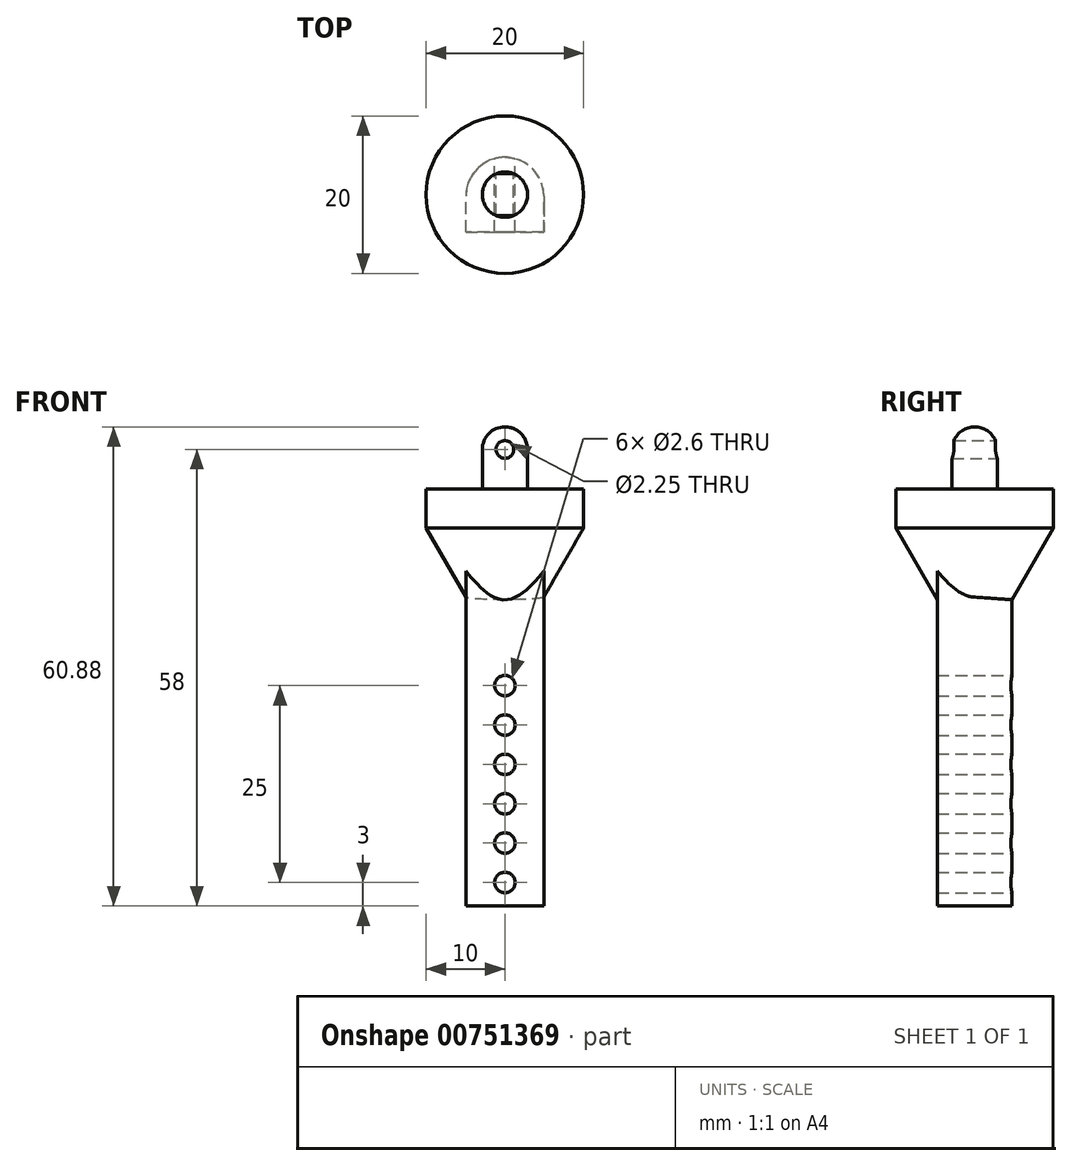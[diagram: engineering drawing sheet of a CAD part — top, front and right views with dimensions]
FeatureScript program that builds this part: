
annotation { "Feature Type Name" : "Feature", "Feature Type Description" : "" }
export const myFeature = defineFeature(function(context is Context, id is Id, definition is map)
    precondition{}
    {
        {
            var Q0;
            Q0=qCreatedBy(makeId("Front.planeOp"),FACE);
            var sketch = newSketch(context, id + "F0", { "sketchPlane" : qUnion([Q0])});
            skLineSegment(sketch, "E0", {"start": v(-4.95, 0) * mm, "end": v(4.95, 0) * mm});
            skPoint(sketch, "E1", {"position": v(0, 0) * mm});
            skLineSegment(sketch, "E2", {"start": v(0, 0) * mm, "end": v(0, 3) * mm, "construction": true});
            skLineSegment(sketch, "E3", {"start": v(0, 3) * mm, "end": v(0, 8) * mm, "construction": true});
            skLineSegment(sketch, "E4", {"start": v(0, 8) * mm, "end": v(0, 13) * mm, "construction": true});
            skLineSegment(sketch, "E5", {"start": v(0, 13) * mm, "end": v(0, 18) * mm, "construction": true});
            skLineSegment(sketch, "E6", {"start": v(0, 18) * mm, "end": v(0, 23) * mm, "construction": true});
            skLineSegment(sketch, "E7", {"start": v(0, 23) * mm, "end": v(0, 28) * mm, "construction": true});
            skLineSegment(sketch, "E8", {"start": v(0, 28) * mm, "end": v(0, 53) * mm, "construction": true});
            skCircle(sketch, "E9", {"center": v(0, 3) * mm, "radius": 1.3 * mm});
            skCircle(sketch, "E10", {"center": v(0, 8) * mm, "radius": 1.3 * mm});
            skCircle(sketch, "E11", {"center": v(0, 13) * mm, "radius": 1.3 * mm});
            skCircle(sketch, "E12", {"center": v(0, 18) * mm, "radius": 1.3 * mm});
            skCircle(sketch, "E13", {"center": v(0, 23) * mm, "radius": 1.3 * mm});
            skCircle(sketch, "E14", {"center": v(0, 28) * mm, "radius": 1.3 * mm});
            skCircle(sketch, "E15", {"center": v(0, 53) * mm, "radius": 1.13 * mm, "construction": true});
            skLineSegment(sketch, "E16", {"start": v(4.95, 0) * mm, "end": v(4.95, 28) * mm});
            skLineSegment(sketch, "E17", {"start": v(4.95, 28) * mm, "end": v(4.95, 33) * mm});
            skLineSegment(sketch, "E18", {"start": v(0, 53) * mm, "end": v(0, 49) * mm, "construction": true});
            skLineSegment(sketch, "E19", {"start": v(-10, 49) * mm, "end": v(10, 49) * mm, "construction": true});
            skPoint(sketch, "E20", {"position": v(0, 49) * mm});
            skLineSegment(sketch, "E21", {"start": v(10, 49) * mm, "end": v(10, 43.83) * mm, "construction": true});
            skLineSegment(sketch, "E22", {"start": v(10, 43.83) * mm, "end": v(4.95, 33) * mm, "construction": true});
            skLineSegment(sketch, "E23", {"start": v(4.95, 33) * mm, "end": v(4.95, 40.7) * mm, "construction": true});
            skLineSegment(sketch, "E24", {"start": v(-2.88, 49) * mm, "end": v(2.88, 49) * mm, "construction": true});
            skLineSegment(sketch, "E25", {"start": v(-2.88, 49) * mm, "end": v(-2.88, 53) * mm, "construction": true});
            skLineSegment(sketch, "E26.MirrorCS", {"start": v(2.88, 49) * mm, "end": v(2.88, 53) * mm, "construction": true});
            skLineSegment(sketch, "E27.MirrorCS", {"start": v(-10, 49) * mm, "end": v(-10, 43.83) * mm, "construction": true});
            skLineSegment(sketch, "E28.MirrorCS", {"start": v(-10, 43.83) * mm, "end": v(-4.95, 33) * mm, "construction": true});
            skLineSegment(sketch, "E29.MirrorCS", {"start": v(-4.95, 28) * mm, "end": v(-4.95, 33) * mm});
            skLineSegment(sketch, "E30.MirrorCS", {"start": v(-4.95, 0) * mm, "end": v(-4.95, 28) * mm});
            skArc(sketch, "E31", {"start": v(2.88, 53) * mm, "mid": v(0, 55.88) * mm, "end": v(-2.88, 53) * mm, "construction": true});
            skLineSegment(sketch, "E32", {"start": v(-4.95, 33) * mm, "end": v(4.95, 33) * mm});
            skSolve(sketch);
        }
        {
            var Q0;
            Q0=makeQuery(id+"F0.imprint","IMPRINT",FACE,{"disambiguationData":[TD([[makeQuery(id+"F0.imprint","IMPRINT",EDGE,{"derivedFrom":sQuery(id+"F0.wireOp",EDGE,"E0")}),1.0]])]});
            extrude(context, id + "F1", {"entities" : qUnion([Q0]), "depth" : 9.5 * mm, "offsetDistance" : 25 * mm});
        }
        {
            var Q0;
            Q0=makeQuery(id+"F1.opExtrude","SWEPT_FACE",FACE,{"disambiguationData":[OSD([sQuery(id+"F0.wireOp",EDGE,"E32")])]});
            var sketch = newSketch(context, id + "F2", { "sketchPlane" : qUnion([Q0])});
            skCircle(sketch, "E33", {"center": v(0, -4.75) * mm, "radius": 10 * mm});
            skPoint(sketch, "E33.centerSnap0", {"position": v(-4.95, -4.75) * mm});
            skCircle(sketch, "E34", {"center": v(0, -4.75) * mm, "radius": 2.88 * mm});
            skSolve(sketch);
        }
        {
            var Q0;
            Q0=makeQuery(id+"F2.imprint","IMPRINT",FACE,{"disambiguationData":[TD([[makeQuery(id+"F2.imprint","IMPRINT",EDGE,{"derivedFrom":sQuery(id+"F2.wireOp",EDGE,"E33")}),1.0]])]});
            var Q1;
            Q1=makeQuery(id+"F2.imprint","IMPRINT",FACE,{"disambiguationData":[TD([[makeQuery(id+"F2.imprint","IMPRINT",EDGE,{"derivedFrom":sQuery(id+"F2.wireOp",EDGE,"E34")}),-1.0]])]});
            extrude(context, id + "F3", {"entities" : qUnion([Q0, Q1]), "operationType" : NewBodyOperationType.ADD, "depth" : 20 * mm, "offsetDistance" : 25 * mm});
        }
        {
            var Q0;
            Q0=makeQuery(id+"F2.imprint","IMPRINT",FACE,{"disambiguationData":[TD([[makeQuery(id+"F2.imprint","IMPRINT",EDGE,{"derivedFrom":sQuery(id+"F2.wireOp",EDGE,"E34")}),1.0]])]});
            extrude(context, id + "F4", {"entities" : qUnion([Q0]), "operationType" : NewBodyOperationType.ADD, "depth" : (25 + (5.75 / 2)) * mm, "offsetDistance" : 25 * mm});
        }
        {
            var Q0;
            Q0=qCreatedBy(makeId("Front.planeOp"),FACE);
            var sketch = newSketch(context, id + "F5", { "sketchPlane" : qUnion([Q0])});
            skLineSegment(sketch, "E35", {"start": v(0, 0) * mm, "end": v(0, 58) * mm, "construction": true});
            skCircle(sketch, "E36", {"center": v(0, 58) * mm, "radius": 1.13 * mm});
            skSolve(sketch);
        }
        {
            var Q0;
            Q0=makeQuery(id+"F5.imprint","IMPRINT",FACE,{"disambiguationData":[TD([[makeQuery(id+"F5.imprint","IMPRINT",EDGE,{"derivedFrom":sQuery(id+"F5.wireOp",EDGE,"E36")}),1.0]])]});
            extrude(context, id + "F6", {"entities" : qUnion([Q0]), "operationType" : NewBodyOperationType.REMOVE, "depth" : 25 * mm, "offsetDistance" : 25 * mm});
        }
        {
            var Q0;
            Q0=makeQuery(id+"F4.opExtrude","CAP_EDGE",EDGE,{"disambiguationData":[OSD([sQuery(id+"F2.wireOp",EDGE,"E34")])],"isStart":false});
            fillet(context, id + "F7", {"entities" : qUnion([Q0]), "radius" : (5.75 / 2) * mm, "tangentPropagation" : true, "allowEdgeOverflow" : false});
        }
        {
            var Q0;
            Q0=makeQuery(id+"F3.opExtrude","CAP_EDGE",EDGE,{"disambiguationData":[OSD([sQuery(id+"F2.wireOp",EDGE,"E33")])],"isStart":true});
            chamfer(context, id + "F8", {"entities" : qUnion([Q0]), "chamferType" : ChamferType.OFFSET_ANGLE, "width" : 15 * mm, "oppositeDirection" : false, "angle" : 30 * degree, "tangentPropagation" : true});
        }
        {
            var Q0;
            Q0=makeQuery(id+"F1.opExtrude","CAP_EDGE",EDGE,{"disambiguationData":[OSD([sQuery(id+"F0.wireOp",EDGE,"E29.MirrorCS"),sQuery(id+"F0.wireOp",EDGE,"E30.MirrorCS")])],"isStart":true});
            var Q1;
            Q1=makeQuery(id+"F1.opExtrude","CAP_EDGE",EDGE,{"disambiguationData":[OSD([sQuery(id+"F0.wireOp",EDGE,"E16"),sQuery(id+"F0.wireOp",EDGE,"E17")])],"isStart":true});
            fillet(context, id + "F9", {"entities" : qUnion([Q0, Q1]), "radius" : (9.9 / 2) * mm, "tangentPropagation" : true, "allowEdgeOverflow" : false});
        }
    });
